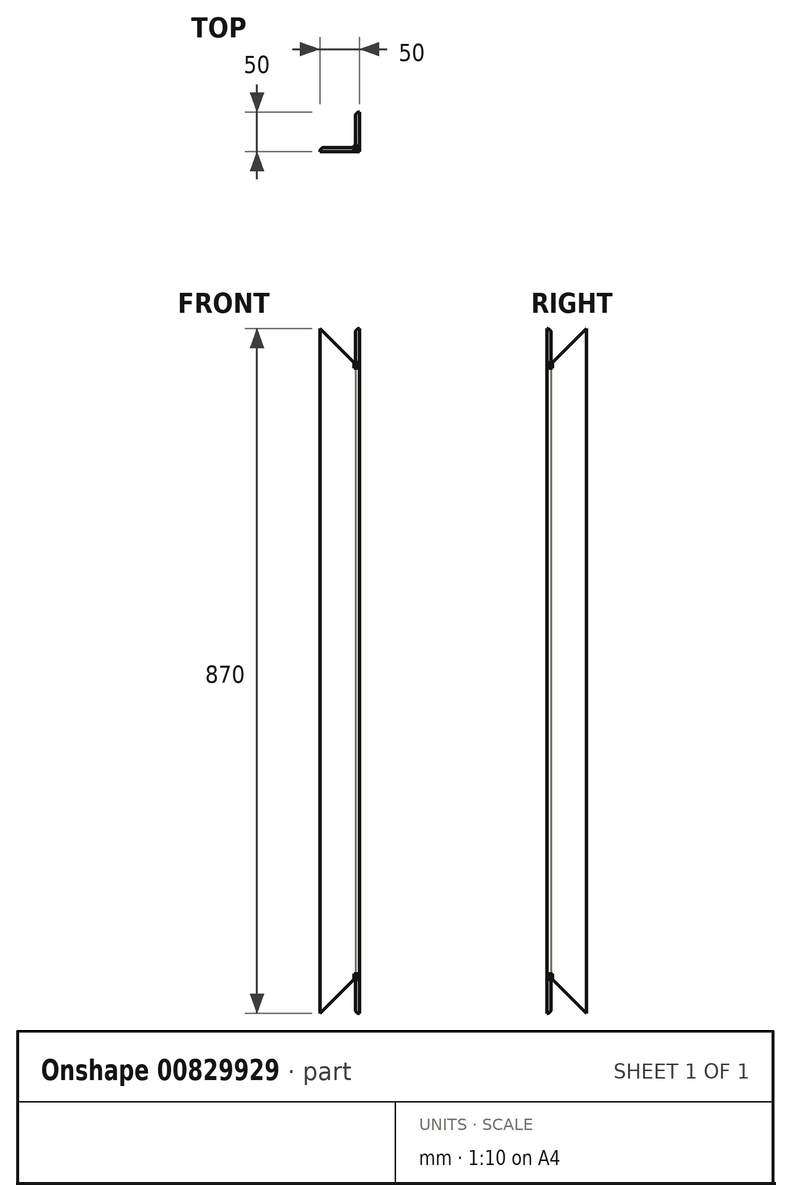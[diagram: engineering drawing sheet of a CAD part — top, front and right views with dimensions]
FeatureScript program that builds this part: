
annotation { "Feature Type Name" : "Feature", "Feature Type Description" : "" }
export const myFeature = defineFeature(function(context is Context, id is Id, definition is map)
    precondition{}
    {
        {
            var Q0;
            Q0=qCreatedBy(makeId("Top.planeOp"),FACE);
            var sketch = newSketch(context, id + "F0", { "sketchPlane" : qUnion([Q0])});
            skLineSegment(sketch, "E0", {"start": v(0, 0) * mm, "end": v(0, 50) * mm});
            skLineSegment(sketch, "E1", {"start": v(0, 0) * mm, "end": v(-50, 0) * mm});
            skLineSegment(sketch, "E2", {"start": v(-50, 0) * mm, "end": v(-50, 0) * mm});
            skLineSegment(sketch, "E3", {"start": v(-45, 5) * mm, "end": v(-10, 5) * mm});
            skLineSegment(sketch, "E4", {"start": v(-5, 10) * mm, "end": v(-5, 45) * mm});
            skLineSegment(sketch, "E5", {"start": v(0, 50) * mm, "end": v(0, 50) * mm});
            skPoint(sketch, "E6.visualSharp", {"position": v(-50, 5) * mm});
            skArc(sketch, "E6.filletArc", {"start": v(-45, 5) * mm, "mid": v(-48.54, 3.54) * mm, "end": v(-50, 0) * mm});
            skPoint(sketch, "E7.visualSharp", {"position": v(-5, 50) * mm});
            skArc(sketch, "E7.filletArc", {"start": v(0, 50) * mm, "mid": v(-3.54, 48.54) * mm, "end": v(-5, 45) * mm});
            skPoint(sketch, "E8.visualSharp", {"position": v(-5, 5) * mm});
            skArc(sketch, "E8.filletArc", {"start": v(-10, 5) * mm, "mid": v(-6.46, 6.46) * mm, "end": v(-5, 10) * mm});
            skSolve(sketch);
        }
        {
            var Q0;
            Q0=makeQuery(id+"F0.imprint","IMPRINT",FACE,{"disambiguationData":[TD([[makeQuery(id+"F0.imprint","IMPRINT",EDGE,{"derivedFrom":sQuery(id+"F0.wireOp",EDGE,"E0")}),1.0]])]});
            extrude(context, id + "F1", {"entities" : qUnion([Q0]), "depth" : (845 + 25) * mm, "offsetDistance" : 25 * mm});
        }
        {
            var Q0;
            Q0=makeQuery(id+"F1.opExtrude","SWEPT_FACE",FACE,{"disambiguationData":[OSD([sQuery(id+"F0.wireOp",EDGE,"E1")])]});
            var sketch = newSketch(context, id + "F2", { "sketchPlane" : qUnion([Q0])});
            skLineSegment(sketch, "E9", {"start": v(-50, 870) * mm, "end": v(0, 820) * mm});
            skLineSegment(sketch, "E10", {"start": v(-50, 0) * mm, "end": v(0, 50) * mm});
            skSolve(sketch);
        }
        {
            var Q0;
            Q0=makeQuery(id+"F1.opExtrude","SWEPT_FACE",FACE,{"disambiguationData":[OSD([sQuery(id+"F0.wireOp",EDGE,"E0")])]});
            var sketch = newSketch(context, id + "F3", { "sketchPlane" : qUnion([Q0])});
            skLineSegment(sketch, "E11", {"start": v(50, 870) * mm, "end": v(0, 820) * mm});
            skSolve(sketch);
        }
        {
            var Q0;
            Q0=makeQuery(id+"F1.opExtrude","SWEPT_FACE",FACE,{"disambiguationData":[OSD([sQuery(id+"F0.wireOp",EDGE,"E0")])]});
            var sketch = newSketch(context, id + "F4", { "sketchPlane" : qUnion([Q0])});
            skLineSegment(sketch, "E12", {"start": v(50, 0) * mm, "end": v(0, 50) * mm});
            skSolve(sketch);
        }
        {
            var Q0;
            Q0=makeQuery(id+"F1.opExtrude","SWEPT_EDGE",EDGE,{"disambiguationData":[OSD([sQuery(id+"F0.wireOp",EDGE,"E0"),sQuery(id+"F0.wireOp",EDGE,"E1")])]});
            cPlane(context, id + "F5", {"entities" : qUnion([Q0]), "cplaneType" : CPlaneType.LINE_ANGLE, "offset" : 25 * mm, "angle" : 45 * degree, "width" : 150 * mm, "height" : 150 * mm});
        }
        {
            var Q0;
            {var subQ0=sQuery(id+"F3.wireOp",EDGE,"E11");Q0=makeQuery(id+"F3.imprint","IMPRINT",FACE,{"disambiguationData":[TD([[makeQuery(id+"F3.imprint","IMPRINT",EDGE,{"derivedFrom":subQ0}),-1.0]])]});}
            var Q1;
            {var subQ0=sQuery(id+"F4.wireOp",EDGE,"E12");Q1=makeQuery(id+"F4.imprint","IMPRINT",FACE,{"disambiguationData":[TD([[makeQuery(id+"F4.imprint","IMPRINT",EDGE,{"derivedFrom":subQ0}),1.0]])]});}
            extrude(context, id + "F6", {"entities" : qUnion([Q0, Q1]), "operationType" : NewBodyOperationType.REMOVE, "oppositeDirection" : true, "depth" : 7 * mm, "offsetDistance" : 25 * mm});
        }
        {
            var Q0;
            {var subQ0=sQuery(id+"F2.wireOp",EDGE,"E9");Q0=makeQuery(id+"F2.imprint","IMPRINT",FACE,{"disambiguationData":[TD([[makeQuery(id+"F2.imprint","IMPRINT",EDGE,{"derivedFrom":subQ0}),1.0]])]});}
            var Q1;
            {var subQ0=sQuery(id+"F2.wireOp",EDGE,"E10");Q1=makeQuery(id+"F2.imprint","IMPRINT",FACE,{"disambiguationData":[TD([[makeQuery(id+"F2.imprint","IMPRINT",EDGE,{"derivedFrom":subQ0}),-1.0]])]});}
            extrude(context, id + "F7", {"entities" : qUnion([Q0, Q1]), "operationType" : NewBodyOperationType.REMOVE, "oppositeDirection" : true, "depth" : 7 * mm, "offsetDistance" : 25 * mm});
        }
    });
